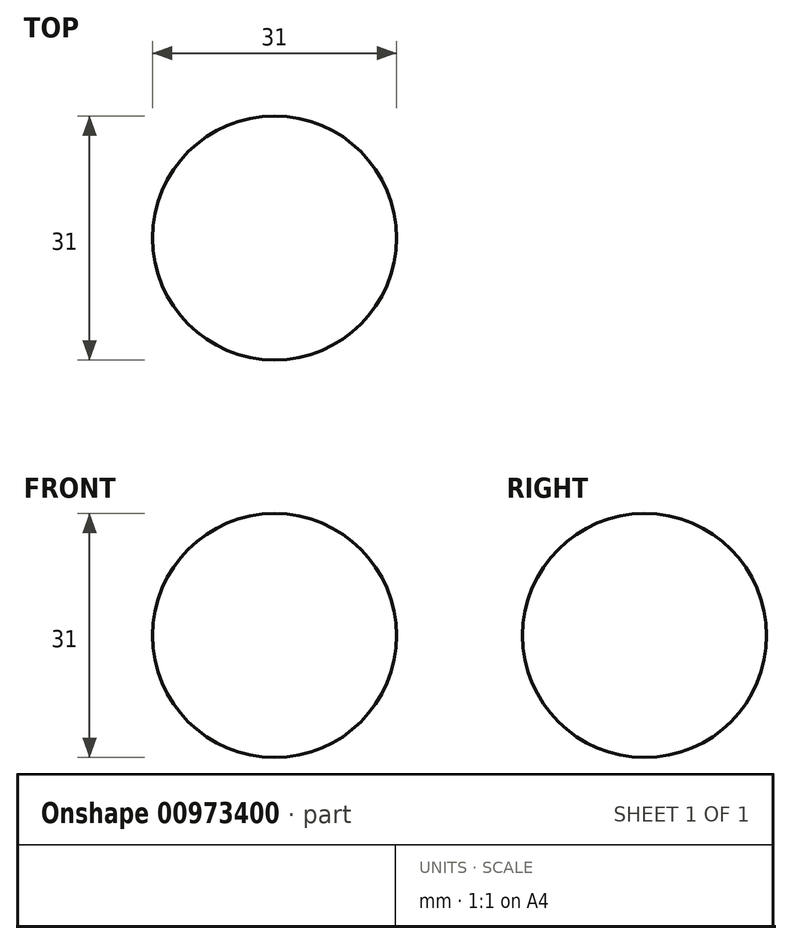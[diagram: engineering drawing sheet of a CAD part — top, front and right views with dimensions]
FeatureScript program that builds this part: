
annotation { "Feature Type Name" : "Feature", "Feature Type Description" : "" }
export const myFeature = defineFeature(function(context is Context, id is Id, definition is map)
    precondition{}
    {
        {
            var Q0;
            Q0=qCreatedBy(makeId("Top.planeOp"),FACE);
            var sketch = newSketch(context, id + "F0", { "sketchPlane" : qUnion([Q0])});
            skCircle(sketch, "E0", {"center": v(0, 0) * mm, "radius": 15.5 * mm});
            skSolve(sketch);
        }
        {
            var Q0;
            Q0=makeQuery(id+"F0.imprint","IMPRINT",FACE,{"disambiguationData":[TD([[makeQuery(id+"F0.imprint","IMPRINT",EDGE,{"derivedFrom":sQuery(id+"F0.wireOp",EDGE,"E0")}),1.0]])]});
            extrude(context, id + "F1", {"entities" : qUnion([Q0]), "depth" : 15.5 * mm, "offsetDistance" : 25 * mm, "hasSecondDirection" : true, "secondDirectionOppositeDirection" : true, "secondDirectionDepth" : 15.5 * mm});
        }
        {
            var Q0;
            Q0=makeQuery(id+"F1.opExtrude","CAP_FACE",FACE,{"disambiguationData":[OSD([sQuery(id+"F0.wireOp",EDGE,"E0")])],"isStart":false});
            var Q1;
            Q1=makeQuery(id+"F1.opExtrude","CAP_EDGE",EDGE,{"disambiguationData":[OSD([sQuery(id+"F0.wireOp",EDGE,"E0")])],"isStart":true});
            fillet(context, id + "F2", {"entities" : qUnion([Q0, Q1]), "radius" : 15.5 * mm, "tangentPropagation" : true, "allowEdgeOverflow" : false});
        }
    });
